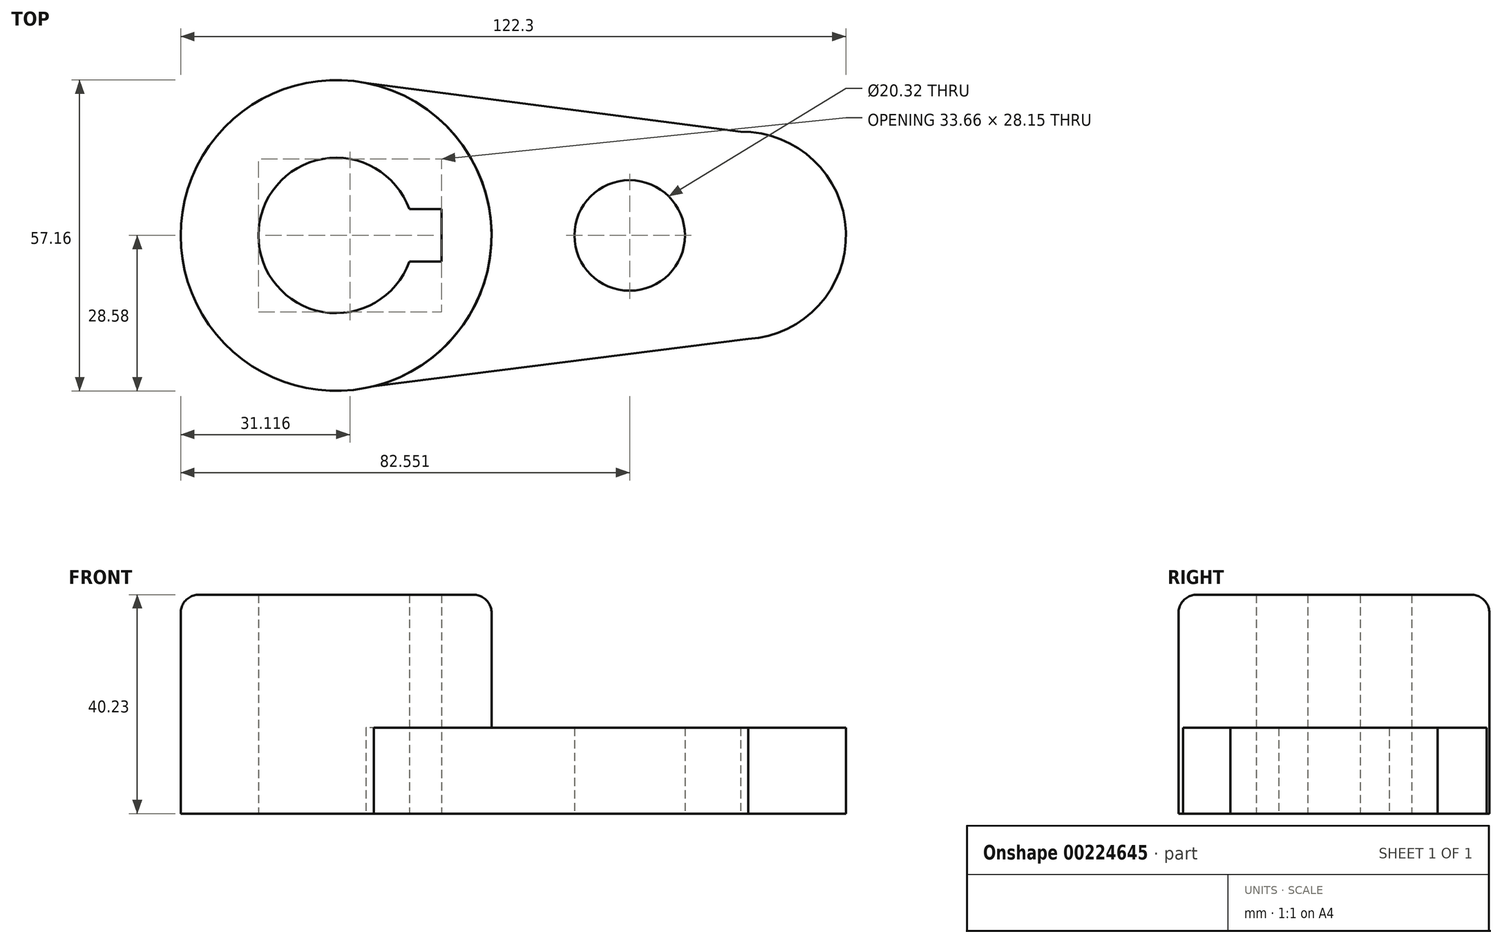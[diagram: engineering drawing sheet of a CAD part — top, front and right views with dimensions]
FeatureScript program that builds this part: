
annotation { "Feature Type Name" : "Feature", "Feature Type Description" : "" }
export const myFeature = defineFeature(function(context is Context, id is Id, definition is map)
    precondition{}
    {
        {
            var Q0;
            Q0=qCreatedBy(makeId("Top.planeOp"),FACE);
            var sketch = newSketch(context, id + "F0", { "sketchPlane" : qUnion([Q0])});
            skLineSegment(sketch, "E0", {"start": v(-39.84, 0) * mm, "end": v(14.13, 0) * mm});
            skCircle(sketch, "E1", {"center": v(-39.84, 0) * mm, "radius": 14.29 * mm});
            skCircle(sketch, "E2", {"center": v(-39.84, 0) * mm, "radius": 28.58 * mm});
            skPoint(sketch, "E3.middle", {"position": v(-25.56, 0) * mm});
            skCircle(sketch, "E4", {"center": v(14.13, 0) * mm, "radius": 10.16 * mm});
            skLineSegment(sketch, "E5.right", {"start": v(-20.48, -4.83) * mm, "end": v(-20.48, 4.83) * mm});
            skPoint(sketch, "E5.middle", {"position": v(-36.88, 0) * mm});
            skLineSegment(sketch, "E6", {"start": v(-20.48, 4.83) * mm, "end": v(-26.4, 4.83) * mm});
            skLineSegment(sketch, "E7", {"start": v(-20.48, -4.83) * mm, "end": v(-26.4, -4.83) * mm});
            skArc(sketch, "E8", {"start": v(34.54, 19.05) * mm, "mid": v(53.87, 0.68) * mm, "end": v(35.9, -19.02) * mm});
            skLineSegment(sketch, "E9", {"start": v(34.54, 19.05) * mm, "end": v(-34.4, 28.05) * mm});
            skLineSegment(sketch, "E10", {"start": v(35.9, -19.02) * mm, "end": v(-32.89, -27.72) * mm});
            skSolve(sketch);
        }
        {
            var Q0;
            Q0=makeQuery(id+"F0.imprint","IMPRINT",FACE,{"disambiguationData":[TD([[makeQuery(id+"F0.imprint","IMPRINT",EDGE,{"derivedFrom":sQuery(id+"F0.wireOp",EDGE,"E4")}),-1.0]])]});
            extrude(context, id + "F1", {"entities" : qUnion([Q0]), "depth" : 15.77 * mm});
        }
        {
            var Q0;
            {var subQ3=sQuery(id+"F0.wireOp",EDGE,"E6");Q0=makeQuery(id+"F0.imprint","IMPRINT",FACE,{"disambiguationData":[TD([[makeQuery(id+"F0.imprint","IMPRINT",EDGE,{"derivedFrom":subQ3}),-1.0]])]});}
            extrude(context, id + "F2", {"entities" : qUnion([Q0]), "operationType" : NewBodyOperationType.ADD, "depth" : 40.23 * mm});
        }
        {
            var Q0;
            Q0=makeQuery(id+"F2.opExtrude","CAP_EDGE",EDGE,{"disambiguationData":[OSD([sQuery(id+"F0.wireOp",EDGE,"E2")])],"isStart":false});
            fillet(context, id + "F3", {"entities" : qUnion([Q0]), "radius" : 3.3 * mm, "tangentPropagation" : true, "allowEdgeOverflow" : false});
        }
    });
